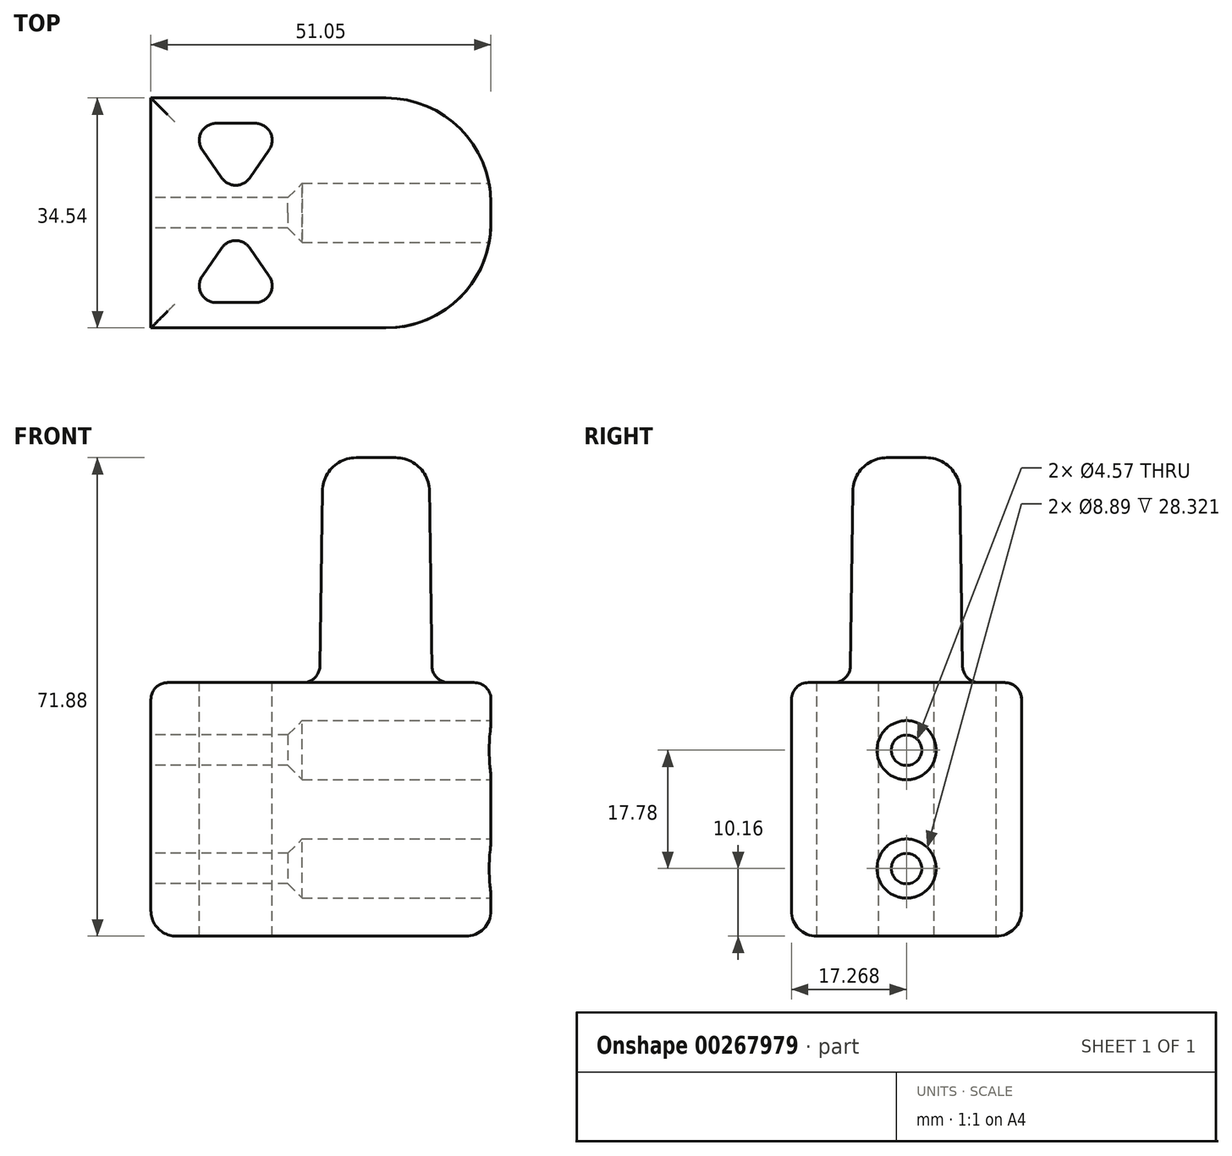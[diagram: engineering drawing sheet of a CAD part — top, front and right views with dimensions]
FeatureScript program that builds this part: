
annotation { "Feature Type Name" : "Feature", "Feature Type Description" : "" }
export const myFeature = defineFeature(function(context is Context, id is Id, definition is map)
    precondition{}
    {
        {
            var Q0;
            Q0=qCreatedBy(makeId("Top.planeOp"),FACE);
            var sketch = newSketch(context, id + "F0", { "sketchPlane" : qUnion([Q0])});
            skLineSegment(sketch, "E0.bottom", {"start": v(0, 0) * mm, "end": v(34.54, 0) * mm});
            skLineSegment(sketch, "E0.top", {"start": v(0, -34.54) * mm, "end": v(34.54, -34.54) * mm});
            skLineSegment(sketch, "E0.left", {"start": v(0, 0) * mm, "end": v(0, -34.54) * mm});
            skLineSegment(sketch, "E0.right", {"start": v(34.54, 0) * mm, "end": v(34.54, -34.54) * mm});
            skSolve(sketch);
        }
        {
            var Q0;
            Q0=qSketchRegion(id+"F0",true);
            extrude(context, id + "F1", {"entities" : qUnion([Q0]), "depth" : 38.1 * mm});
        }
        {
            var Q0;
            Q0=makeQuery(id+"F1.opExtrude","CAP_FACE",FACE,{"disambiguationData":[OSD([sQuery(id+"F0.wireOp",EDGE,"E0.bottom"),sQuery(id+"F0.wireOp",EDGE,"E0.top"),sQuery(id+"F0.wireOp",EDGE,"E0.left"),sQuery(id+"F0.wireOp",EDGE,"E0.right")])],"isStart":false});
            var sketch = newSketch(context, id + "F2", { "sketchPlane" : qUnion([Q0])});
            skCircle(sketch, "E1", {"center": v(17.27, -17.27) * mm, "radius": 8.45 * mm});
            skPoint(sketch, "E1.centerSnap0", {"position": v(17.27, -34.54) * mm});
            skPoint(sketch, "E1.centerSnap1", {"position": v(34.54, -17.27) * mm});
            skSolve(sketch);
        }
        {
            var Q0;
            Q0=makeQuery(id+"F1.opExtrude","SWEPT_EDGE",EDGE,{"disambiguationData":[OSD([sQuery(id+"F0.wireOp",EDGE,"E0.top"),sQuery(id+"F0.wireOp",EDGE,"E0.right")])]});
            var Q1;
            Q1=makeQuery(id+"F1.opExtrude","SWEPT_EDGE",EDGE,{"disambiguationData":[OSD([sQuery(id+"F0.wireOp",EDGE,"E0.bottom"),sQuery(id+"F0.wireOp",EDGE,"E0.right")])]});
            fillet(context, id + "F3", {"entities" : qUnion([Q0, Q1]), "radius" : 15.75 * mm, "tangentPropagation" : true, "allowEdgeOverflow" : false});
        }
        {
            var Q0;
            Q0=makeQuery(id+"F1.opExtrude","SWEPT_FACE",FACE,{"disambiguationData":[OSD([sQuery(id+"F0.wireOp",EDGE,"E0.left")])]});
            var sketch = newSketch(context, id + "F4", { "sketchPlane" : qUnion([Q0])});
            skCircle(sketch, "E2", {"center": v(17.27, 10.16) * mm, "radius": 2.29 * mm});
            skPoint(sketch, "E2.centerSnap0", {"position": v(17.27, 0) * mm});
            skCircle(sketch, "E3", {"center": v(17.27, 27.94) * mm, "radius": 2.29 * mm});
            skPoint(sketch, "E3.centerSnap0", {"position": v(17.27, 38.1) * mm});
            skSolve(sketch);
        }
        {
            var Q0;
            Q0=qSketchRegion(id+"F4",true);
            extrude(context, id + "F5", {"entities" : qUnion([Q0]), "operationType" : NewBodyOperationType.REMOVE, "endBound" : BoundingType.THROUGH_ALL, "oppositeDirection" : true, "depth" : 25.4 * mm});
        }
        {
            var Q0;
            {var subQ0=sQuery(id+"F0.wireOp",EDGE,"E0.right");Q0=makeQuery(id+"F5.boolean.opBoolean","SPLIT",FACE,{"disambiguationData":[TD([makeQuery(id+"F3.opFillet","BLEND_FACE",FACE,{"disambiguationData":[OSD([sQuery(id+"F0.wireOp",EDGE,"E0.bottom"),subQ0])]}),makeQuery(id+"F3.opFillet","BLEND_FACE",FACE,{"disambiguationData":[OSD([sQuery(id+"F0.wireOp",EDGE,"E0.top"),subQ0])]}),makeQuery(id+"F5.opExtrude","SWEPT_FACE",FACE,{"disambiguationData":[OSD([sQuery(id+"F4.wireOp",EDGE,"E2")])]}),makeQuery(id+"F5.opExtrude","SWEPT_FACE",FACE,{"disambiguationData":[OSD([sQuery(id+"F4.wireOp",EDGE,"E3")])]})])],"derivedFrom":makeQuery(id+"F1.opExtrude","SWEPT_FACE",FACE,{"disambiguationData":[OSD([subQ0])]})});}
            var sketch = newSketch(context, id + "F6", { "sketchPlane" : qUnion([Q0])});
            skCircle(sketch, "E4", {"center": v(-17.27, 27.94) * mm, "radius": 4.45 * mm});
            skCircle(sketch, "E5", {"center": v(-17.27, 10.16) * mm, "radius": 4.45 * mm});
            skSolve(sketch);
        }
        {
            var Q0;
            Q0=qSketchRegion(id+"F6",true);
            extrude(context, id + "F7", {"entities" : qUnion([Q0]), "operationType" : NewBodyOperationType.REMOVE, "oppositeDirection" : true, "depth" : 27.94 * mm});
        }
        {
            var Q0;
            Q0=makeQuery(id+"F7.boolean.opBoolean","INTERSECT",EDGE,{"derivedFrom":[makeQuery(id+"F5.boolean.opBoolean","COPY",FACE,{"disambiguationData":[TD([makeQuery(id+"F1.opExtrude","SWEPT_FACE",FACE,{"disambiguationData":[OSD([sQuery(id+"F0.wireOp",EDGE,"E0.left")])]})])],"derivedFrom":makeQuery(id+"F5.opExtrude","SWEPT_FACE",FACE,{"disambiguationData":[OSD([sQuery(id+"F4.wireOp",EDGE,"E3")])]})}),makeQuery(id+"F7.opExtrude","CAP_FACE",FACE,{"disambiguationData":[OSD([sQuery(id+"F6.wireOp",EDGE,"E4")])],"isStart":false})]});
            var Q1;
            Q1=makeQuery(id+"F7.boolean.opBoolean","INTERSECT",EDGE,{"derivedFrom":[makeQuery(id+"F5.boolean.opBoolean","COPY",FACE,{"disambiguationData":[TD([makeQuery(id+"F1.opExtrude","SWEPT_FACE",FACE,{"disambiguationData":[OSD([sQuery(id+"F0.wireOp",EDGE,"E0.left")])]})])],"derivedFrom":makeQuery(id+"F5.opExtrude","SWEPT_FACE",FACE,{"disambiguationData":[OSD([sQuery(id+"F4.wireOp",EDGE,"E2")])]})}),makeQuery(id+"F7.opExtrude","CAP_FACE",FACE,{"disambiguationData":[OSD([sQuery(id+"F6.wireOp",EDGE,"E5")])],"isStart":false})]});
            chamfer(context, id + "F8", {"entities" : qUnion([Q0, Q1]), "width" : 2.54 * mm, "tangentPropagation" : true});
        }
        {
            var Q0;
            Q0=makeQuery(id+"F1.opExtrude","SWEPT_FACE",FACE,{"disambiguationData":[OSD([sQuery(id+"F0.wireOp",EDGE,"E0.left")])]});
            extrude(context, id + "F9", {"entities" : qUnion([Q0]), "operationType" : NewBodyOperationType.ADD, "depth" : 16.5 * mm});
        }
        {
            var Q0;
            Q0=qSketchRegion(id+"F2",true);
            extrude(context, id + "F10", {"entities" : qUnion([Q0]), "operationType" : NewBodyOperationType.ADD, "depth" : 33.78 * mm, "hasDraft" : true, "draftAngle" : .8 * degree, "draftPullDirection" : true});
        }
        {
            var Q0;
            Q0=makeQuery(id+"F1.opExtrude","CAP_FACE",FACE,{"disambiguationData":[OSD([sQuery(id+"F0.wireOp",EDGE,"E0.bottom"),sQuery(id+"F0.wireOp",EDGE,"E0.top"),sQuery(id+"F0.wireOp",EDGE,"E0.left"),sQuery(id+"F0.wireOp",EDGE,"E0.right")])],"isStart":false});
            fillet(context, id + "F11", {"entities" : qUnion([Q0]), "radius" : 2.54 * mm, "tangentPropagation" : true, "allowEdgeOverflow" : false});
        }
        {
            var Q0;
            Q0=makeQuery(id+"F1.opExtrude","CAP_FACE",FACE,{"disambiguationData":[OSD([sQuery(id+"F0.wireOp",EDGE,"E0.bottom"),sQuery(id+"F0.wireOp",EDGE,"E0.top"),sQuery(id+"F0.wireOp",EDGE,"E0.left"),sQuery(id+"F0.wireOp",EDGE,"E0.right")])],"isStart":true});
            fillet(context, id + "F12", {"entities" : qUnion([Q0]), "radius" : 3.8 * mm, "tangentPropagation" : true, "allowEdgeOverflow" : false});
        }
        {
            var Q0;
            Q0=makeQuery(id+"F10.opExtrude","CAP_FACE",FACE,{"disambiguationData":[OSD([sQuery(id+"F2.wireOp",EDGE,"E1")])],"isStart":false});
            fillet(context, id + "F13", {"entities" : qUnion([Q0]), "radius" : 5.08 * mm, "tangentPropagation" : true, "allowEdgeOverflow" : false});
        }
        {
            var Q0;
            {var subQ0=sQuery(id+"F0.wireOp",EDGE,"E0.left");Q0=makeQuery(id+"F9.boolean.opBoolean","MERGE",FACE,{"derivedFrom":[makeQuery(id+"F1.opExtrude","CAP_FACE",FACE,{"disambiguationData":[OSD([sQuery(id+"F0.wireOp",EDGE,"E0.bottom"),sQuery(id+"F0.wireOp",EDGE,"E0.top"),subQ0,sQuery(id+"F0.wireOp",EDGE,"E0.right")])],"isStart":false}),makeQuery(id+"F9.opExtrude","SWEPT_FACE",FACE,{"disambiguationData":[OSD([subQ0]),TDD([makeQuery(id+"F1.opExtrude","CAP_EDGE",EDGE,{"disambiguationData":[OSD([subQ0])],"isStart":false})])]})]});}
            var sketch = newSketch(context, id + "F14", { "sketchPlane" : qUnion([Q0])});
            skLineSegment(sketch, "E6", {"start": v(6.43, -18.8) * mm, "end": v(6.43, -2.54) * mm, "construction": true});
            skLineSegment(sketch, "E7", {"start": v(6.43, -2.54) * mm, "end": v(-13.97, -32) * mm, "construction": true});
            skLineSegment(sketch, "E8", {"start": v(-13.97, -32) * mm, "end": v(-13.97, -2.54) * mm, "construction": true});
            skLineSegment(sketch, "E9", {"start": v(-13.97, -2.54) * mm, "end": v(6.43, -32) * mm, "construction": true});
            skLineSegment(sketch, "E10", {"start": v(6.43, -32) * mm, "end": v(6.43, -2.54) * mm, "construction": true});
            skLineSegment(sketch, "E11", {"start": v(-13.97, -2.54) * mm, "end": v(6.43, -2.54) * mm, "construction": true});
            skLineSegment(sketch, "E12", {"start": v(-13.97, -32) * mm, "end": v(6.43, -32) * mm, "construction": true});
            skLineSegment(sketch, "E13", {"start": v(-8.79, -7.8) * mm, "end": v(-5.86, -12.02) * mm});
            skLineSegment(sketch, "E14", {"start": v(-6.7, -3.81) * mm, "end": v(-0.84, -3.81) * mm});
            skLineSegment(sketch, "E15", {"start": v(1.24, -7.8) * mm, "end": v(-1.68, -12.02) * mm});
            skPoint(sketch, "E16.visualSharp", {"position": v(-11.55, -3.81) * mm});
            skArc(sketch, "E16.filletArc", {"start": v(-6.7, -3.81) * mm, "mid": v(-8.95, -5.17) * mm, "end": v(-8.79, -7.8) * mm});
            skPoint(sketch, "E17.visualSharp", {"position": v(4, -3.81) * mm});
            skArc(sketch, "E17.filletArc", {"start": v(1.24, -7.8) * mm, "mid": v(1.4, -5.17) * mm, "end": v(-0.84, -3.81) * mm});
            skPoint(sketch, "E18.visualSharp", {"position": v(-3.77, -15.04) * mm});
            skArc(sketch, "E18.filletArc", {"start": v(-5.86, -12.02) * mm, "mid": v(-3.77, -13.12) * mm, "end": v(-1.68, -12.02) * mm});
            skLineSegment(sketch, "E19", {"start": v(-3.77, -17.27) * mm, "end": v(-13.97, -17.27) * mm, "construction": true});
            skArc(sketch, "E20.MirrorCS", {"start": v(-5.86, -22.52) * mm, "mid": v(-3.77, -21.43) * mm, "end": v(-1.68, -22.52) * mm});
            skLineSegment(sketch, "E21.MirrorCS", {"start": v(-8.79, -26.75) * mm, "end": v(-5.86, -22.52) * mm});
            skArc(sketch, "E22.MirrorCS", {"start": v(-6.7, -30.73) * mm, "mid": v(-8.95, -29.37) * mm, "end": v(-8.79, -26.75) * mm});
            skLineSegment(sketch, "E23.MirrorCS", {"start": v(-6.7, -30.73) * mm, "end": v(-0.84, -30.73) * mm});
            skArc(sketch, "E24.MirrorCS", {"start": v(1.24, -26.75) * mm, "mid": v(1.4, -29.37) * mm, "end": v(-0.84, -30.73) * mm});
            skLineSegment(sketch, "E25.MirrorCS", {"start": v(1.24, -26.75) * mm, "end": v(-1.68, -22.52) * mm});
            skSolve(sketch);
        }
        {
            var Q0;
            Q0 = qSketchRegion(id + "F14", true);
            extrude(context, id + "F15", {"entities" : qUnion([Q0]), "operationType" : NewBodyOperationType.REMOVE, "endBound" : BoundingType.THROUGH_ALL, "oppositeDirection" : true, "depth" : 25.4 * mm});
        }
    });
